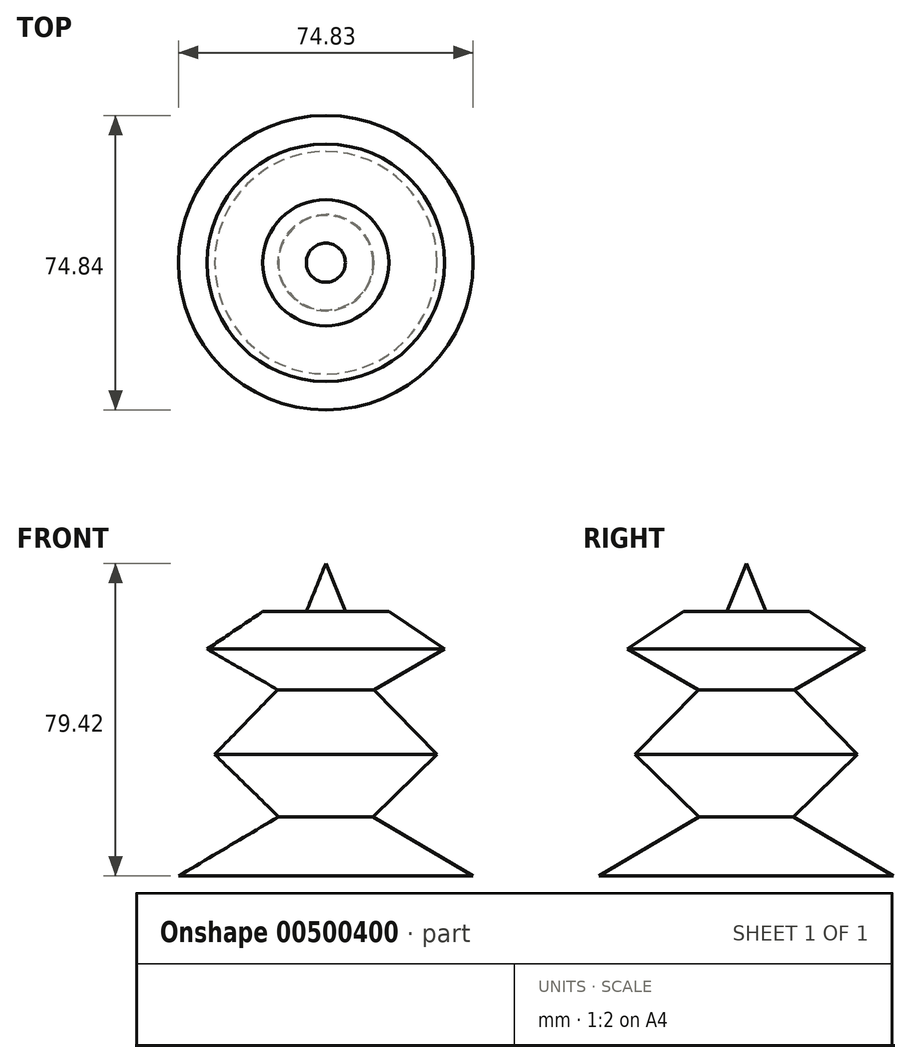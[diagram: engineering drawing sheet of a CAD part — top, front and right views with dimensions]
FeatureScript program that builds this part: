
annotation { "Feature Type Name" : "Feature", "Feature Type Description" : "" }
export const myFeature = defineFeature(function(context is Context, id is Id, definition is map)
    precondition{}
    {
        {
            var Q0;
            Q0=qCreatedBy(makeId("Front.planeOp"),FACE);
            var sketch = newSketch(context, id + "F0", { "sketchPlane" : qUnion([Q0])});
            skLineSegment(sketch, "E0", {"start": v(-45.05, 55.17) * mm, "end": v(-59.18, 45.63) * mm});
            skLineSegment(sketch, "E1", {"start": v(-59.18, 45.63) * mm, "end": v(-41.23, 35.32) * mm});
            skLineSegment(sketch, "E2", {"start": v(-41.23, 35.32) * mm, "end": v(-57.27, 18.9) * mm});
            skLineSegment(sketch, "E3", {"start": v(-57.27, 18.9) * mm, "end": v(-41.03, 3.04) * mm});
            skLineSegment(sketch, "E4", {"start": v(-41.03, 3.04) * mm, "end": v(-66.43, -12.03) * mm});
            skLineSegment(sketch, "E5", {"start": v(-66.43, -12.03) * mm, "end": v(-29.02, -12.03) * mm});
            skLineSegment(sketch, "E6", {"start": v(-29.02, -12.03) * mm, "end": v(-29.02, 67.39) * mm});
            skLineSegment(sketch, "E7", {"start": v(-45.05, 55.17) * mm, "end": v(-33.98, 55.17) * mm});
            skLineSegment(sketch, "E8", {"start": v(-29.02, 67.39) * mm, "end": v(-33.98, 55.17) * mm});
            skSolve(sketch);
        }
        {
            var Q0;
            Q0=makeQuery(id+"F0.imprint","IMPRINT",FACE,{"disambiguationData":[TD([[makeQuery(id+"F0.imprint","IMPRINT",EDGE,{"derivedFrom":sQuery(id+"F0.wireOp",EDGE,"E0")}),1.0]])]});
            var Q1;
            Q1=sQuery(id+"F0.wireOp",EDGE,"E6");
            revolve(context, id + "F1", {"entities" : qUnion([Q0]), "axis" : qUnion([Q1]), "revolveType" : RevolveType.FULL});
        }
    });
